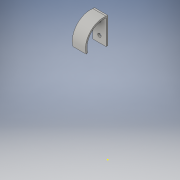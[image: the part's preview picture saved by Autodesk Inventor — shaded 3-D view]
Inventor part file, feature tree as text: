
AUTODESK INVENTOR PART (.ipt)
format: ipt  version: 2016 (Build 200138000, 138)  size: 187,392 bytes
history: native  units: in
note: dims shown in document units (in); Inventor stores cm internally (conversion verified against a paired STEP export)
features: sketch x8, extrude x7
ambient origin geometry x8: Origin, YZ Plane, XZ Plane, XY Plane, X Axis, Y Axis, Z Axis, Center Point
bodies: Solid1 (feature_tree)
feature tree (15):
  extrude  "Extrusion1"  Depth=1.0in
  extrude  "Extrusion2"  Depth=0.5in
  extrude  "Extrusion3"  Depth=0.125in
  sketch  "Sketch4"  dims[d8=9.0in d9=0.0in d11=2.0in]
  extrude  "Extrusion4"  Depth=2.0in
  extrude  "Extrusion5"  Depth=0.125in
  extrude  "Extrusion6"  Depth=1.0in
  extrude  "Extrusion7"  Depth=0.125in
  sketch  "Sketch1"  dims[d0=9.5in d1=1.0in]
  sketch  "Sketch2"  dims[d3=0.5in d4=0.5in]
  sketch  "Sketch3"  dims[d5=1.0in d6=0.0in d7=0.125in]
  sketch  "Sketch5"  dims[d13=0.125in d15=0.125in]
  sketch  "Sketch6"  dims[d16=1.0in d17=0.0in d18=1.75in]
  sketch  "Sketch7"  dims[d19=1.5in d20=0.125in]
  sketch  "Sketch8"  dims[d21=0.125in d22=1.0in d23=0.0in d25=0.5in d26=0.5in d27=0.5in d28=1.0in d29=0.0in d30=1.0in d31=0.0in d32=0.25in d33=0.5in d34=0.5in d35=1.5in d36=0.125in d37=0.0in]
